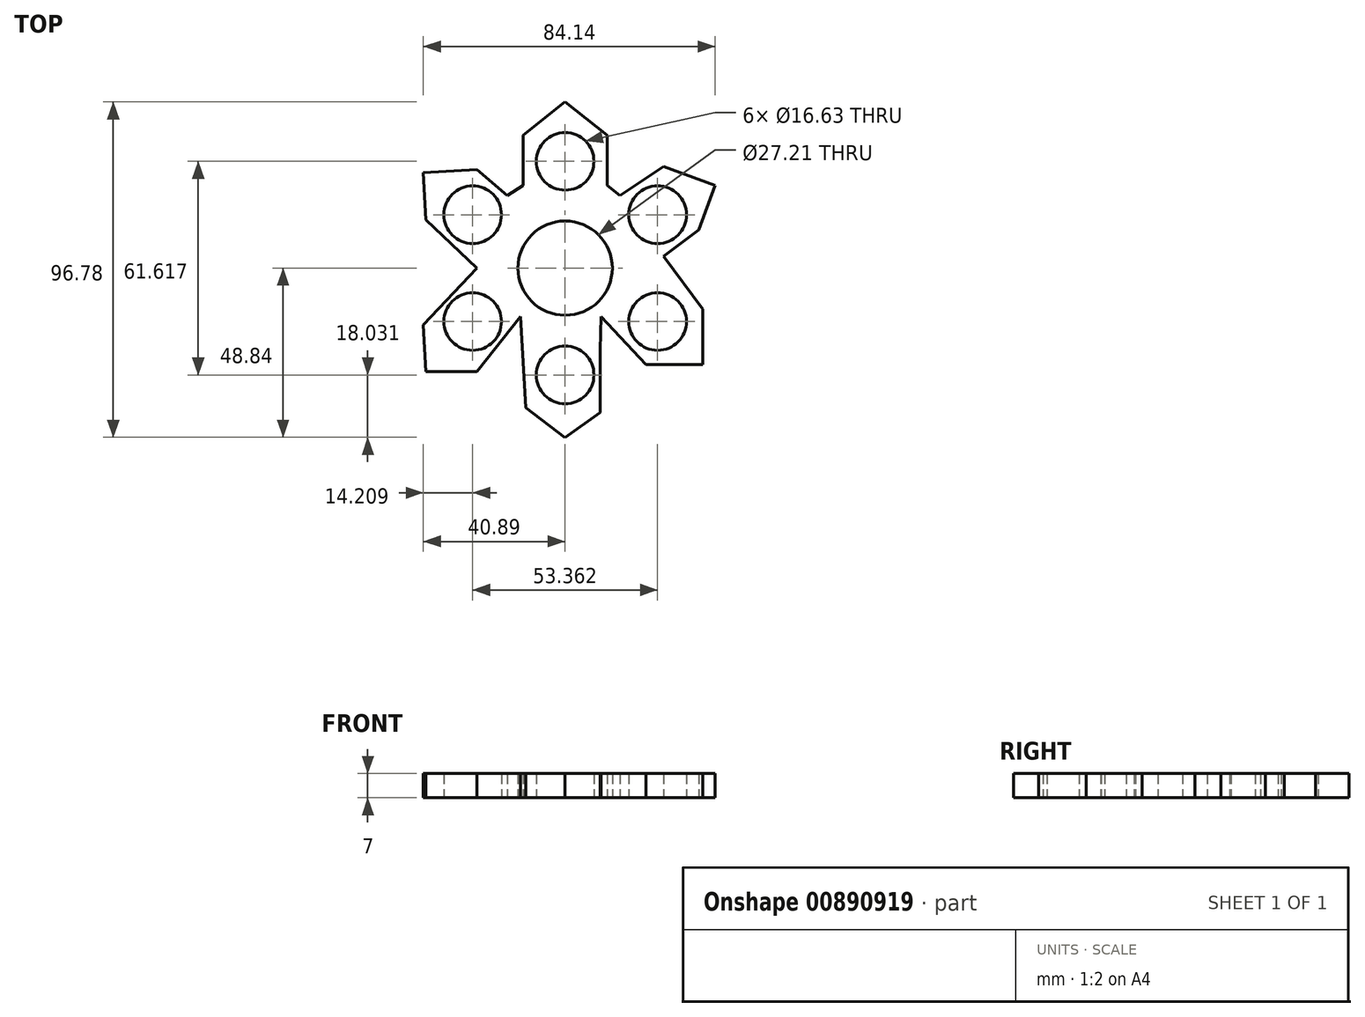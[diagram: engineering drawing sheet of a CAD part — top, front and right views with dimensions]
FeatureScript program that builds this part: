
annotation { "Feature Type Name" : "Feature", "Feature Type Description" : "" }
export const myFeature = defineFeature(function(context is Context, id is Id, definition is map)
    precondition{}
    {
        {
            var Q0;
            Q0=qCreatedBy(makeId("Top.planeOp"),FACE);
            var sketch = newSketch(context, id + "F0", { "sketchPlane" : qUnion([Q0])});
            skCircle(sketch, "E0", {"center": v(0, 0) * mm, "radius": 11.3 * mm});
            skCircle(sketch, "E1", {"center": v(0, 0) * mm, "radius": 13.6 * mm});
            skCircle(sketch, "E2", {"center": v(0, 30.8) * mm, "radius": 8.31 * mm});
            skCircle(sketch, "E3.1.0", {"center": v(-26.68, 15.4) * mm, "radius": 8.31 * mm});
            skCircle(sketch, "E3.2.0", {"center": v(-26.68, -15.4) * mm, "radius": 8.31 * mm});
            skCircle(sketch, "E3.3.0", {"center": v(0, -30.8) * mm, "radius": 8.31 * mm});
            skCircle(sketch, "E3.4.0", {"center": v(26.68, -15.4) * mm, "radius": 8.31 * mm});
            skCircle(sketch, "E3.5.0", {"center": v(26.68, 15.4) * mm, "radius": 8.31 * mm});
            skLineSegment(sketch, "E4", {"start": v(-12.17, 29.3) * mm, "end": v(-12.17, 38.32) * mm});
            skLineSegment(sketch, "E5", {"start": v(-12.17, 38.32) * mm, "end": v(0, 47.94) * mm});
            skLineSegment(sketch, "E6", {"start": v(0, 47.94) * mm, "end": v(12.17, 38.32) * mm});
            skLineSegment(sketch, "E7", {"start": v(12.17, 38.32) * mm, "end": v(12.17, 23.9) * mm});
            skLineSegment(sketch, "E8", {"start": v(-12.17, 29.3) * mm, "end": v(-12.17, 23.9) * mm});
            skLineSegment(sketch, "E9", {"start": v(15.78, 20.89) * mm, "end": v(28.4, 29.3) * mm});
            skLineSegment(sketch, "E10", {"start": v(28.4, 29.3) * mm, "end": v(43.25, 23.9) * mm});
            skLineSegment(sketch, "E11", {"start": v(43.25, 23.9) * mm, "end": v(38.56, 11.02) * mm});
            skLineSegment(sketch, "E12", {"start": v(38.56, 11.02) * mm, "end": v(28.4, 3.46) * mm});
            skLineSegment(sketch, "E13", {"start": v(28.4, 3.46) * mm, "end": v(39.76, -11.78) * mm});
            skLineSegment(sketch, "E14", {"start": v(39.76, -11.78) * mm, "end": v(39.76, -27.8) * mm});
            skLineSegment(sketch, "E15", {"start": v(39.76, -27.8) * mm, "end": v(23.3, -27.8) * mm});
            skLineSegment(sketch, "E16", {"start": v(23.3, -27.8) * mm, "end": v(10.37, -13.98) * mm});
            skLineSegment(sketch, "E17", {"start": v(12.17, 23.9) * mm, "end": v(15.78, 20.89) * mm});
            skLineSegment(sketch, "E18", {"start": v(-12.17, -25.7) * mm, "end": v(-11.35, -40.31) * mm});
            skLineSegment(sketch, "E19", {"start": v(10.07, -23.6) * mm, "end": v(10.07, -41.63) * mm});
            skLineSegment(sketch, "E20", {"start": v(10.07, -41.63) * mm, "end": v(0, -48.84) * mm});
            skLineSegment(sketch, "E21", {"start": v(-11.35, -40.31) * mm, "end": v(0, -48.84) * mm});
            skLineSegment(sketch, "E22", {"start": v(10.07, -23.6) * mm, "end": v(10.37, -13.98) * mm});
            skLineSegment(sketch, "E23", {"start": v(-12.17, -25.7) * mm, "end": v(-12.84, -13.98) * mm});
            skLineSegment(sketch, "E24", {"start": v(-12.84, -13.98) * mm, "end": v(-25.4, -29.9) * mm});
            skLineSegment(sketch, "E25", {"start": v(-25.4, -29.9) * mm, "end": v(-40.13, -29.9) * mm});
            skLineSegment(sketch, "E26", {"start": v(-40.13, -29.9) * mm, "end": v(-40.9, -16.36) * mm});
            skLineSegment(sketch, "E27", {"start": v(-40.9, -16.36) * mm, "end": v(-25.4, 0) * mm});
            skLineSegment(sketch, "E28", {"start": v(-25.4, 0) * mm, "end": v(-40.13, 13.95) * mm});
            skLineSegment(sketch, "E29", {"start": v(-40.13, 13.95) * mm, "end": v(-40.9, 27.5) * mm});
            skLineSegment(sketch, "E30", {"start": v(-40.9, 27.5) * mm, "end": v(-25.4, 28.38) * mm});
            skLineSegment(sketch, "E31", {"start": v(-25.4, 28.38) * mm, "end": v(-16.68, 20.89) * mm});
            skLineSegment(sketch, "E32", {"start": v(-16.68, 20.89) * mm, "end": v(-12.17, 23.9) * mm});
            skSolve(sketch);
        }
        {
            var Q0;
            Q0 = qSketchRegion(id + "F0", true);
            extrude(context, id + "F1", {"entities" : qUnion([Q0]), "depth" : 7 * mm, "offsetDistance" : 25 * mm});
        }
    });
